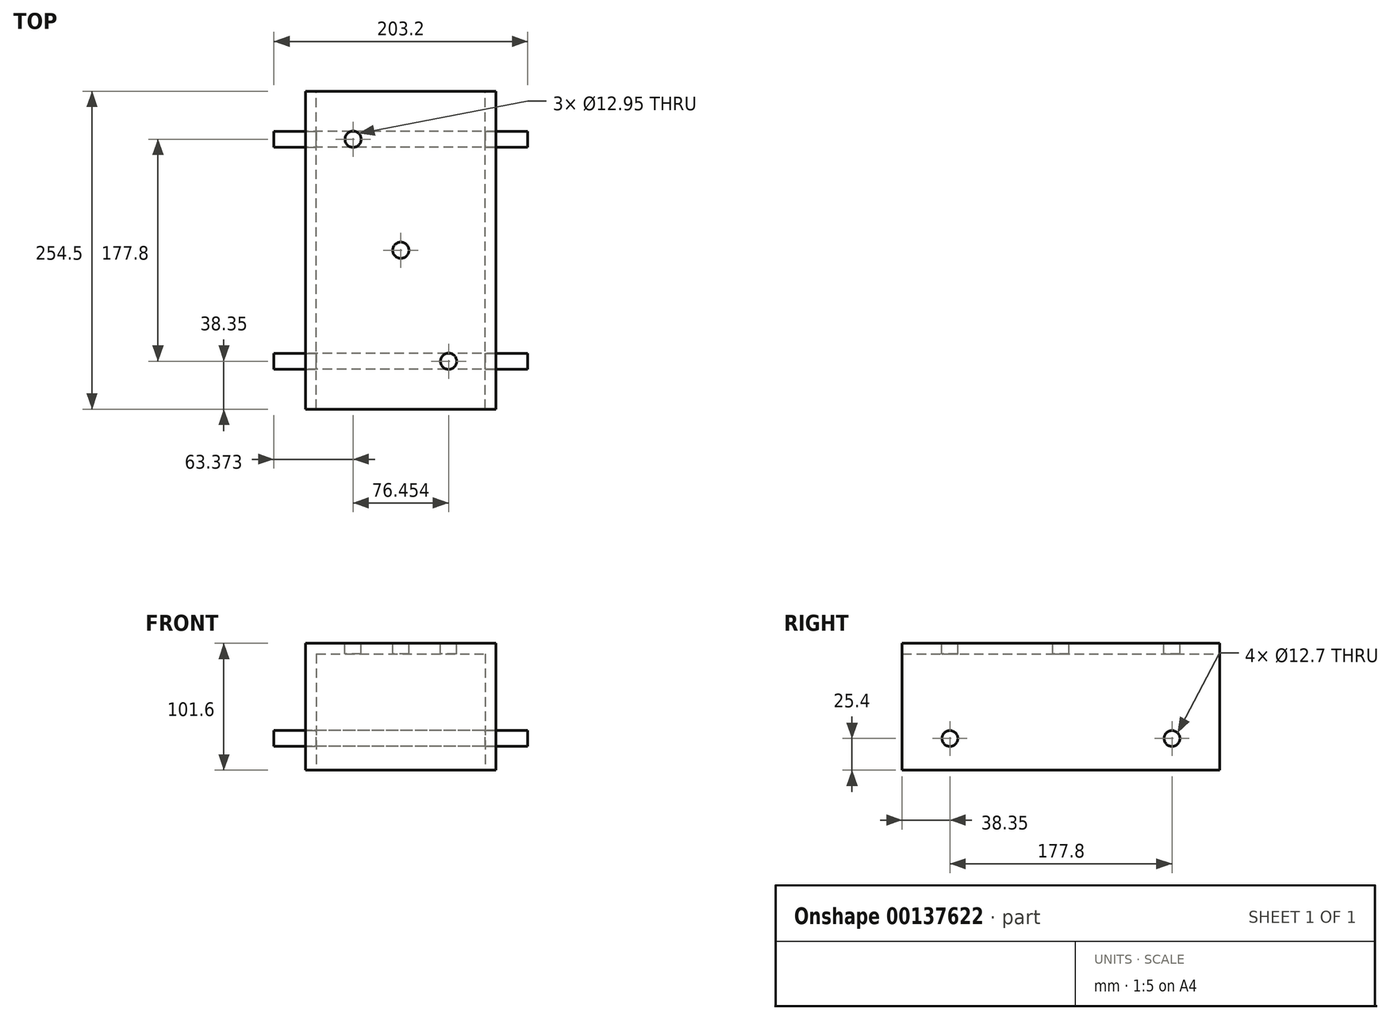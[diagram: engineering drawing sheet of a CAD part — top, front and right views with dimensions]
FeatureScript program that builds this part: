
annotation { "Feature Type Name" : "Feature", "Feature Type Description" : "" }
export const myFeature = defineFeature(function(context is Context, id is Id, definition is map)
    precondition{}
    {
        {
            var Q0;
            Q0=qCreatedBy(makeId("Front.planeOp"),FACE);
            var sketch = newSketch(context, id + "F0", { "sketchPlane" : qUnion([Q0])});
            skLineSegment(sketch, "E0.bottom", {"start": v(-76.2, 50.8) * mm, "end": v(76.2, 50.8) * mm});
            skLineSegment(sketch, "E0.top", {"start": v(-76.2, -50.8) * mm, "end": v(76.2, -50.8) * mm});
            skLineSegment(sketch, "E0.left", {"start": v(-76.2, 50.8) * mm, "end": v(-76.2, -50.8) * mm});
            skLineSegment(sketch, "E0.right", {"start": v(76.2, 50.8) * mm, "end": v(76.2, -50.8) * mm});
            skLineSegment(sketch, "E1.bottom", {"start": v(-67.56, 42.16) * mm, "end": v(67.56, 42.16) * mm});
            skLineSegment(sketch, "E1.top", {"start": v(-67.56, -42.16) * mm, "end": v(67.56, -42.16) * mm});
            skLineSegment(sketch, "E1.left", {"start": v(-67.56, 42.16) * mm, "end": v(-67.56, -42.16) * mm});
            skLineSegment(sketch, "E1.right", {"start": v(67.56, 42.16) * mm, "end": v(67.56, -42.16) * mm});
            skLineSegment(sketch, "E2", {"start": v(0, 42.16) * mm, "end": v(0, -42.16) * mm, "construction": true});
            skLineSegment(sketch, "E3", {"start": v(0, 42.16) * mm, "end": v(0, 50.8) * mm, "construction": true});
            skLineSegment(sketch, "E4", {"start": v(0, -42.16) * mm, "end": v(0, -50.8) * mm, "construction": true});
            skLineSegment(sketch, "E5", {"start": v(0, 0) * mm, "end": v(-67.56, 0) * mm, "construction": true});
            skLineSegment(sketch, "E6", {"start": v(0, 0) * mm, "end": v(67.56, 0) * mm, "construction": true});
            skLineSegment(sketch, "E7", {"start": v(-67.56, 0) * mm, "end": v(-76.2, 0) * mm, "construction": true});
            skLineSegment(sketch, "E8", {"start": v(67.56, 0) * mm, "end": v(76.2, 0) * mm, "construction": true});
            skSolve(sketch);
        }
        {
            var Q0;
            Q0=makeQuery(id+"F0.imprint","IMPRINT",FACE,{"disambiguationData":[TD([[makeQuery(id+"F0.imprint","IMPRINT",EDGE,{"derivedFrom":sQuery(id+"F0.wireOp",EDGE,"E0.bottom")}),-1.0]])]});
            extrude(context, id + "F1", {"entities" : qUnion([Q0]), "endBound" : BoundingType.SYMMETRIC, "depth" : 254 * mm});
        }
        {
            var Q0;
            Q0=makeQuery(id+"F1.opExtrude","SWEPT_FACE",FACE,{"disambiguationData":[OSD([sQuery(id+"F0.wireOp",EDGE,"E0.right")])]});
            var sketch = newSketch(context, id + "F2", { "sketchPlane" : qUnion([Q0])});
            skLineSegment(sketch, "E9", {"start": v(0, 0) * mm, "end": v(0, -25.4) * mm, "construction": true});
            skLineSegment(sketch, "E10", {"start": v(-88.9, -25.4) * mm, "end": v(88.9, -25.4) * mm, "construction": true});
            skCircle(sketch, "E11", {"center": v(-88.9, -25.4) * mm, "radius": 6.35 * mm});
            skCircle(sketch, "E12", {"center": v(88.9, -25.4) * mm, "radius": 6.35 * mm});
            skCircle(sketch, "E13", {"center": v(88.9, -25.4) * mm, "radius": 38.1 * mm, "construction": true});
            skCircle(sketch, "E14", {"center": v(-88.9, -25.4) * mm, "radius": 38.1 * mm, "construction": true});
            skSolve(sketch);
        }
        {
            var Q0;
            Q0=qSketchRegion(id+"F2",true);
            extrude(context, id + "F3", {"entities" : qUnion([Q0]), "operationType" : NewBodyOperationType.REMOVE, "endBound" : BoundingType.THROUGH_ALL, "oppositeDirection" : true, "depth" : 25.4 * mm});
        }
        {
            var Q0;
            Q0=qCreatedBy(makeId("Right.planeOp"),FACE);
            var sketch = newSketch(context, id + "F4", { "sketchPlane" : qUnion([Q0])});
            skCircle(sketch, "E15.0", {"center": v(-88.9, -25.4) * mm, "radius": 6.35 * mm});
            skCircle(sketch, "E16.0", {"center": v(88.9, -25.4) * mm, "radius": 6.35 * mm});
            skSolve(sketch);
        }
        {
            var Q0;
            Q0=makeQuery(id+"F4.imprint","IMPRINT",FACE,{"disambiguationData":[TD([[makeQuery(id+"F4.imprint","IMPRINT",EDGE,{"derivedFrom":sQuery(id+"F4.wireOp",EDGE,"E15.0")}),1.0]])]});
            var Q1;
            Q1=makeQuery(id+"F4.imprint","IMPRINT",FACE,{"disambiguationData":[TD([[makeQuery(id+"F4.imprint","IMPRINT",EDGE,{"derivedFrom":sQuery(id+"F4.wireOp",EDGE,"E16.0")}),1.0]])]});
            extrude(context, id + "F5", {"entities" : qUnion([Q0, Q1]), "endBound" : BoundingType.SYMMETRIC, "depth" : 203.2 * mm});
        }
        {
            var Q0;
            Q0=makeQuery(id+"F1.opExtrude","SWEPT_FACE",FACE,{"disambiguationData":[OSD([sQuery(id+"F0.wireOp",EDGE,"E1.top")])]});
            var sketch = newSketch(context, id + "F6", { "sketchPlane" : qUnion([Q0])});
            skSolve(sketch);
        }
        {
            var Q0;
            {var subQ0=sQuery(id+"F0.wireOp",EDGE,"E1.top");Q0=makeQuery(id+"F6.imprint","IMPRINT",FACE,{"disambiguationData":[TD([[makeQuery(id+"F6.imprint","IMPRINT",EDGE,{"derivedFrom":makeQuery(id+"F1.opExtrude","CAP_EDGE",EDGE,{"disambiguationData":[OSD([subQ0])],"isStart":true})}),-1.0]])]});}
            extrude(context, id + "F7", {"entities" : qUnion([Q0]), "operationType" : NewBodyOperationType.REMOVE, "oppositeDirection" : true, "depth" : 25.4 * mm});
        }
        {
            var Q0;
            Q0=makeQuery(id+"F1.opExtrude","SWEPT_FACE",FACE,{"disambiguationData":[OSD([sQuery(id+"F0.wireOp",EDGE,"E0.bottom")])]});
            var sketch = newSketch(context, id + "F8", { "sketchPlane" : qUnion([Q0])});
            skCircle(sketch, "E17", {"center": v(-38.23, 88.9) * mm, "radius": 6.48 * mm});
            skCircle(sketch, "E18", {"center": v(38.23, -88.9) * mm, "radius": 6.48 * mm});
            skLineSegment(sketch, "E19", {"start": v(-38.23, 88.9) * mm, "end": v(38.23, 88.9) * mm, "construction": true});
            skLineSegment(sketch, "E20", {"start": v(0, -88.9) * mm, "end": v(0, 88.9) * mm, "construction": true});
            skCircle(sketch, "E21", {"center": v(0, 0) * mm, "radius": 6.48 * mm});
            skLineSegment(sketch, "E22", {"start": v(-38.23, -88.9) * mm, "end": v(38.23, -88.9) * mm, "construction": true});
            skCircle(sketch, "E23", {"center": v(0, 0) * mm, "radius": 63.5 * mm, "construction": true});
            skCircle(sketch, "E24", {"center": v(-38.23, 88.9) * mm, "radius": 25.4 * mm, "construction": true});
            skCircle(sketch, "E25", {"center": v(38.23, -88.9) * mm, "radius": 25.4 * mm, "construction": true});
            skSolve(sketch);
        }
        {
            var Q0;
            Q0=qSketchRegion(id+"F8",true);
            extrude(context, id + "F9", {"entities" : qUnion([Q0]), "operationType" : NewBodyOperationType.REMOVE, "oppositeDirection" : true, "depth" : 25.4 * mm});
        }
        {
            var Q0;
            Q0=makeQuery(id+"F1.opExtrude","CAP_FACE",FACE,{"disambiguationData":[OSD([sQuery(id+"F0.wireOp",EDGE,"E0.bottom"),sQuery(id+"F0.wireOp",EDGE,"E0.top"),sQuery(id+"F0.wireOp",EDGE,"E0.left"),sQuery(id+"F0.wireOp",EDGE,"E0.right"),sQuery(id+"F0.wireOp",EDGE,"E1.bottom"),sQuery(id+"F0.wireOp",EDGE,"E1.top"),sQuery(id+"F0.wireOp",EDGE,"E1.left"),sQuery(id+"F0.wireOp",EDGE,"E1.right")])],"isStart":true});
            var sketch = newSketch(context, id + "F10", { "sketchPlane" : qUnion([Q0])});
            skLineSegment(sketch, "E26.bottom", {"start": v(-76.2, 50.8) * mm, "end": v(76.2, 50.8) * mm});
            skLineSegment(sketch, "E26.top", {"start": v(-76.2, -50.8) * mm, "end": v(76.2, -50.8) * mm});
            skLineSegment(sketch, "E26.left", {"start": v(-76.2, 50.8) * mm, "end": v(-76.2, -50.8) * mm});
            skLineSegment(sketch, "E26.right", {"start": v(76.2, 50.8) * mm, "end": v(76.2, -50.8) * mm});
            skSolve(sketch);
        }
        {
            var Q0;
            Q0 = qSketchRegion(id + "F10", true);
            extrude(context, id + "F11", {"entities" : qUnion([Q0]), "operationType" : NewBodyOperationType.ADD, "depth" : 0.25 * mm});
        }
        {
            var Q0;
            Q0=makeQuery(id+"F1.opExtrude","CAP_FACE",FACE,{"disambiguationData":[OSD([sQuery(id+"F0.wireOp",EDGE,"E0.bottom"),sQuery(id+"F0.wireOp",EDGE,"E0.top"),sQuery(id+"F0.wireOp",EDGE,"E0.left"),sQuery(id+"F0.wireOp",EDGE,"E0.right"),sQuery(id+"F0.wireOp",EDGE,"E1.bottom"),sQuery(id+"F0.wireOp",EDGE,"E1.top"),sQuery(id+"F0.wireOp",EDGE,"E1.left"),sQuery(id+"F0.wireOp",EDGE,"E1.right")])],"isStart":false});
            var sketch = newSketch(context, id + "F12", { "sketchPlane" : qUnion([Q0])});
            skLineSegment(sketch, "E27.bottom", {"start": v(76.2, 50.8) * mm, "end": v(-76.2, 50.8) * mm});
            skLineSegment(sketch, "E27.top", {"start": v(76.2, -50.8) * mm, "end": v(-76.2, -50.8) * mm});
            skLineSegment(sketch, "E27.left", {"start": v(76.2, 50.8) * mm, "end": v(76.2, -50.8) * mm});
            skLineSegment(sketch, "E27.right", {"start": v(-76.2, 50.8) * mm, "end": v(-76.2, -50.8) * mm});
            skSolve(sketch);
        }
        {
            var Q0;
            Q0 = qSketchRegion(id + "F12", true);
            extrude(context, id + "F13", {"entities" : qUnion([Q0]), "operationType" : NewBodyOperationType.ADD, "depth" : 0.25 * mm});
        }
    });
